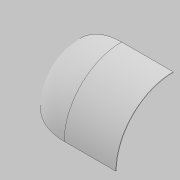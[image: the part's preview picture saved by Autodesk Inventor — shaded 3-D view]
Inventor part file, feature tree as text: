
AUTODESK INVENTOR PART (.ipt)
format: ipt  version: 2021 (Build 250183000, 183)  size: 127,488 bytes
history: native  units: mm
features: sketch x2, revolve x1, extrude x1, other x1
ambient origin geometry x8: Origin, YZ Plane, XZ Plane, XY Plane, X Axis, Y Axis, Z Axis, Center Point
bodies: Body1 (feature_tree)
feature tree (5):
  revolve  "Revolution1"  [1 undecoded]
  extrude  "Extrusion2"  TaperAngle=0.0deg  [1 undecoded]
  other  "tangent1"
  sketch  "Sketch1"  dims[d0=10.0mm d1=1000.0mm]
  sketch  "Sketch2"  dims[d2=0.0mm d3=0.0mm d6=90.0deg d9=900.0mm d10=0.0mm]
note: 2 required parameter values undecoded (feature->parameter linkage not recoverable at this tier; creation-order binding heuristic only, values carry confidence <= 0.55)